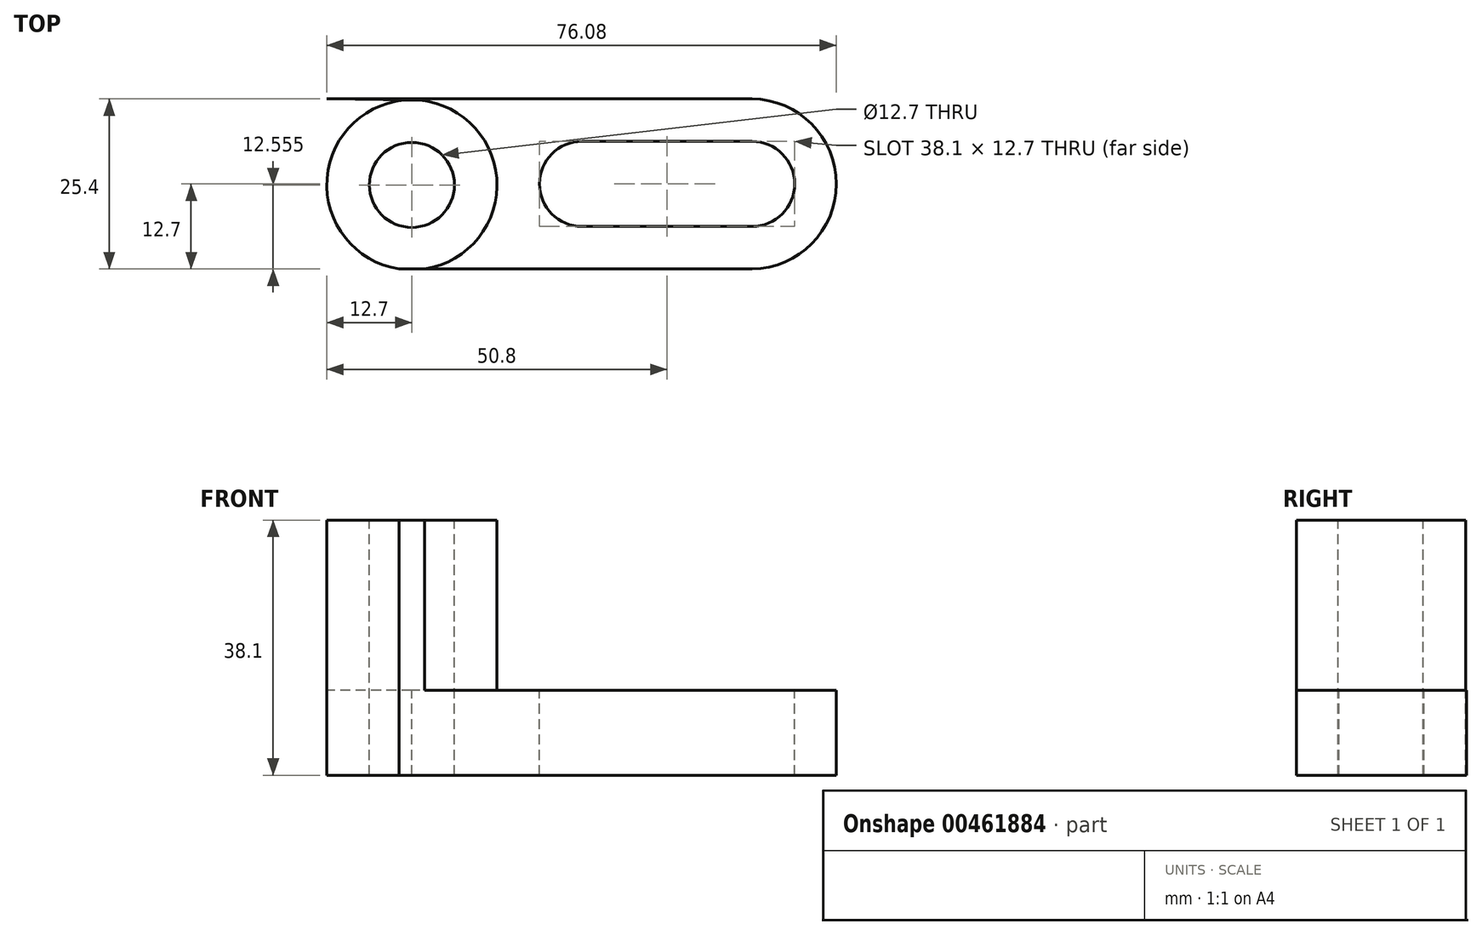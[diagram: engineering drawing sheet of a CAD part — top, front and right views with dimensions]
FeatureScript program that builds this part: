
annotation { "Feature Type Name" : "Feature", "Feature Type Description" : "" }
export const myFeature = defineFeature(function(context is Context, id is Id, definition is map)
    precondition{}
    {
        {
            var Q0;
            Q0=qCreatedBy(makeId("Front.planeOp"),FACE);
            var sketch = newSketch(context, id + "F0", { "sketchPlane" : qUnion([Q0])});
            skLineSegment(sketch, "E0", {"start": v(0, 0) * mm, "end": v(76.2, 0) * mm});
            skLineSegment(sketch, "E1", {"start": v(76.2, 0) * mm, "end": v(76.2, 12.7) * mm});
            skLineSegment(sketch, "E2", {"start": v(76.2, 12.7) * mm, "end": v(25.4, 12.7) * mm});
            skLineSegment(sketch, "E3", {"start": v(25.4, 12.7) * mm, "end": v(25.4, 38.1) * mm});
            skLineSegment(sketch, "E4", {"start": v(25.4, 38.1) * mm, "end": v(0, 38.1) * mm});
            skLineSegment(sketch, "E5", {"start": v(0, 38.1) * mm, "end": v(0, 0) * mm});
            skSolve(sketch);
        }
        {
            var Q0;
            Q0=makeQuery(id+"F0.imprint","IMPRINT",FACE,{"disambiguationData":[TD([[makeQuery(id+"F0.imprint","IMPRINT",EDGE,{"derivedFrom":sQuery(id+"F0.wireOp",EDGE,"E0")}),1.0]])]});
            extrude(context, id + "F1", {"entities" : qUnion([Q0]), "depth" : 25.4 * mm});
        }
        {
            var Q0;
            Q0=makeQuery(id+"F1.opExtrude","SWEPT_FACE",FACE,{"disambiguationData":[OSD([sQuery(id+"F0.wireOp",EDGE,"E4")])]});
            var sketch = newSketch(context, id + "F2", { "sketchPlane" : qUnion([Q0])});
            skCircle(sketch, "E6", {"center": v(12.7, -12.84) * mm, "radius": 12.7 * mm});
            skSolve(sketch);
        }
        {
            var Q0;
            {var subQ1=sQuery(id+"F0.wireOp",EDGE,"E4");var subQ6=makeQuery(id+"F1.opExtrude","CAP_EDGE",EDGE,{"disambiguationData":[OSD([subQ1])],"isStart":true});Q0=makeQuery(id+"F2.imprint","IMPRINT",FACE,{"disambiguationData":[TD([[makeQuery(id+"F2.imprint","IMPRINT",EDGE,{"derivedFrom":subQ6}),1.0]])]});}
            var Q1;
            {var subQ0=sQuery(id+"F2.wireOp",EDGE,"E6");var subQ1=sQuery(id+"F0.wireOp",EDGE,"E4");var subQ4=makeQuery(id+"F1.opExtrude","CAP_EDGE",EDGE,{"disambiguationData":[OSD([subQ1])],"isStart":false});var subQ5=makeQuery(id+"F2.imprint","INTERSECT",VERTEX,{"disambiguationData":[OD(1.0)],"derivedFrom":[subQ4,subQ0]});Q1=makeQuery(id+"F2.imprint","IMPRINT",FACE,{"disambiguationData":[TD([[makeQuery(id+"F2.imprint","IMPRINT",EDGE,{"disambiguationData":[TD([[subQ5,-1.0]])],"derivedFrom":subQ0}),-1.0]])]});}
            extrude(context, id + "F3", {"entities" : qUnion([Q0, Q1]), "operationType" : NewBodyOperationType.REMOVE, "oppositeDirection" : true, "depth" : 25.4 * mm});
        }
        {
            var Q0;
            Q0=makeQuery(id+"F1.opExtrude","SWEPT_FACE",FACE,{"disambiguationData":[OSD([sQuery(id+"F0.wireOp",EDGE,"E4")])]});
            var sketch = newSketch(context, id + "F4", { "sketchPlane" : qUnion([Q0])});
            skCircle(sketch, "E7", {"center": v(12.7, -12.84) * mm, "radius": 12.7 * mm});
            skLineSegment(sketch, "E8", {"start": v(12.7, -25.4) * mm, "end": v(0, -25.4) * mm});
            skLineSegment(sketch, "E9", {"start": v(0, -25.4) * mm, "end": v(0, 0) * mm});
            skLineSegment(sketch, "E10", {"start": v(0, 0) * mm, "end": v(12.7, -0.14) * mm});
            skSolve(sketch);
        }
        {
            var Q0;
            {var subQ3=sQuery(id+"F4.wireOp",EDGE,"E10");Q0=makeQuery(id+"F4.imprint","IMPRINT",FACE,{"disambiguationData":[TD([[makeQuery(id+"F4.imprint","IMPRINT",EDGE,{"derivedFrom":subQ3}),-1.0]])]});}
            var Q1;
            {var subQ0=sQuery(id+"F4.wireOp",EDGE,"E9");var subQ1=sQuery(id+"F4.wireOp",EDGE,"E7");var subQ2=makeQuery(id+"F4.imprint","INTERSECT",VERTEX,{"derivedFrom":[subQ1,subQ0]});Q1=makeQuery(id+"F4.imprint","IMPRINT",FACE,{"disambiguationData":[TD([[makeQuery(id+"F4.imprint","IMPRINT",EDGE,{"disambiguationData":[TD([[subQ2,-1.0]])],"derivedFrom":subQ1}),-1.0]])]});}
            extrude(context, id + "F5", {"entities" : qUnion([Q0, Q1]), "operationType" : NewBodyOperationType.REMOVE, "oppositeDirection" : true, "depth" : 38.1 * mm});
        }
        {
            var Q0;
            {var subQ0=sQuery(id+"F2.wireOp",EDGE,"E6");var subQ1=sQuery(id+"F0.wireOp",EDGE,"E4");var subQ2=sQuery(id+"F0.wireOp",EDGE,"E3");Q0=makeQuery(id+"F3.boolean.opBoolean","MERGE",FACE,{"derivedFrom":[makeQuery(id+"F1.opExtrude","SWEPT_FACE",FACE,{"disambiguationData":[OSD([sQuery(id+"F0.wireOp",EDGE,"E2")])]}),makeQuery(id+"F3.opExtrude","CAP_FACE",FACE,{"disambiguationData":[OSD([subQ2,subQ1,sQuery(id+"F0.wireOp",EDGE,"E5"),subQ0])],"isStart":false}),makeQuery(id+"F3.opExtrude","CAP_FACE",FACE,{"disambiguationData":[OSD([subQ2,subQ1,subQ0])],"isStart":false})]});}
            var sketch = newSketch(context, id + "F6", { "sketchPlane" : qUnion([Q0])});
            skCircle(sketch, "E11", {"center": v(63.5, -12.7) * mm, "radius": 6.35 * mm});
            skCircle(sketch, "E12", {"center": v(38.1, -12.7) * mm, "radius": 6.35 * mm});
            skLineSegment(sketch, "E13", {"start": v(38.1, -6.35) * mm, "end": v(63.5, -6.35) * mm});
            skLineSegment(sketch, "E14", {"start": v(63.5, -19.05) * mm, "end": v(38.1, -19.05) * mm});
            skArc(sketch, "E15", {"start": v(63.5, -25.4) * mm, "mid": v(76.08, -12.7) * mm, "end": v(63.5, 0) * mm});
            skSolve(sketch);
        }
        {
            var Q0;
            {var subQ0=sQuery(id+"F6.wireOp",EDGE,"E12");var subQ1=makeQuery(id+"F6.imprint","INTERSECT",VERTEX,{"derivedFrom":[subQ0,sQuery(id+"F6.wireOp",EDGE,"E13")]});Q0=makeQuery(id+"F6.imprint","IMPRINT",FACE,{"disambiguationData":[TD([[makeQuery(id+"F6.imprint","IMPRINT",EDGE,{"disambiguationData":[TD([[subQ1,-1.0]])],"derivedFrom":subQ0}),1.0]])]});}
            var Q1;
            {var subQ0=sQuery(id+"F6.wireOp",EDGE,"E13");Q1=makeQuery(id+"F6.imprint","IMPRINT",FACE,{"disambiguationData":[TD([[makeQuery(id+"F6.imprint","IMPRINT",EDGE,{"derivedFrom":subQ0}),-1.0]])]});}
            var Q2;
            {var subQ0=sQuery(id+"F6.wireOp",EDGE,"E11");var subQ1=makeQuery(id+"F6.imprint","INTERSECT",VERTEX,{"derivedFrom":[subQ0,sQuery(id+"F6.wireOp",EDGE,"E13")]});Q2=makeQuery(id+"F6.imprint","IMPRINT",FACE,{"disambiguationData":[TD([[makeQuery(id+"F6.imprint","IMPRINT",EDGE,{"disambiguationData":[TD([[subQ1,-1.0]])],"derivedFrom":subQ0}),1.0]])]});}
            var Q3;
            {var subQ0=sQuery(id+"F6.wireOp",EDGE,"E15");Q3=makeQuery(id+"F6.imprint","IMPRINT",FACE,{"disambiguationData":[TD([[makeQuery(id+"F6.imprint","IMPRINT",EDGE,{"derivedFrom":subQ0}),-1.0]])]});}
            extrude(context, id + "F7", {"entities" : qUnion([Q0, Q1, Q2, Q3]), "operationType" : NewBodyOperationType.REMOVE, "oppositeDirection" : true, "depth" : 12.7 * mm});
        }
        {
            var Q0;
            Q0=makeQuery(id+"F1.opExtrude","SWEPT_FACE",FACE,{"disambiguationData":[OSD([sQuery(id+"F0.wireOp",EDGE,"E4")])]});
            var sketch = newSketch(context, id + "F8", { "sketchPlane" : qUnion([Q0])});
            skCircle(sketch, "E16", {"center": v(12.7, -12.84) * mm, "radius": 6.35 * mm});
            skSolve(sketch);
        }
        {
            var Q0;
            Q0=makeQuery(id+"F8.imprint","IMPRINT",FACE,{"disambiguationData":[TD([[makeQuery(id+"F8.imprint","IMPRINT",EDGE,{"derivedFrom":sQuery(id+"F8.wireOp",EDGE,"E16")}),1.0]])]});
            extrude(context, id + "F9", {"entities" : qUnion([Q0]), "operationType" : NewBodyOperationType.REMOVE, "oppositeDirection" : true, "depth" : 38.1 * mm});
        }
    });
